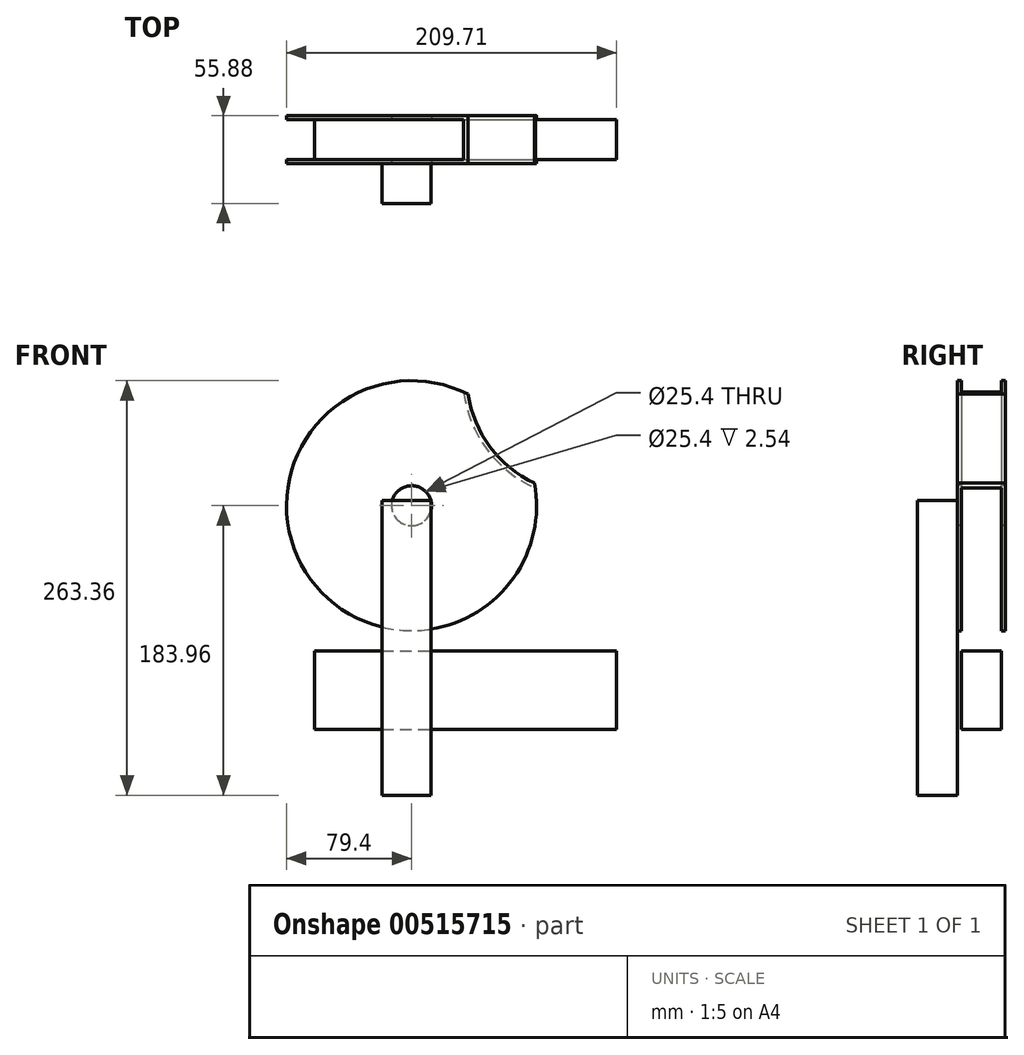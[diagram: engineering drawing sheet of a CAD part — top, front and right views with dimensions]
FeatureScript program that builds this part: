
annotation { "Feature Type Name" : "Feature", "Feature Type Description" : "" }
export const myFeature = defineFeature(function(context is Context, id is Id, definition is map)
    precondition{}
    {
        {
            var Q0;
            Q0=qCreatedBy(makeId("Front.planeOp"),FACE);
            var sketch = newSketch(context, id + "F0", { "sketchPlane" : qUnion([Q0])});
            skCircle(sketch, "E0", {"center": v(0, 0) * mm, "radius": 76.98 * mm});
            skSolve(sketch);
        }
        {
            var Q0;
            Q0 = qSketchRegion(id + "F0", true);
            var sketch = newSketch(context, id + "F1", { "sketchPlane" : qUnion([Q0])});
            skCircle(sketch, "E1", {"center": v(-109.51, -81.83) * mm, "radius": 79.4 * mm});
            skSolve(sketch);
        }
        {
            var Q0;
            {var subQ0=sQuery(id+"F1.wireOp",EDGE,"E1");var subQ1=makeQuery(id+"F0.imprint","IMPRINT",EDGE,{"derivedFrom":sQuery(id+"F0.wireOp",EDGE,"E0")});var subQ2=makeQuery(id+"F1.imprint","INTERSECT",VERTEX,{"disambiguationData":[OD(0.0)],"derivedFrom":[subQ1,subQ0]});Q0=makeQuery(id+"F1.imprint","IMPRINT",FACE,{"disambiguationData":[TD([[makeQuery(id+"F1.imprint","IMPRINT",EDGE,{"disambiguationData":[TD([[subQ2,-1.0]])],"derivedFrom":subQ0}),1.0]])]});}
            var sketch = newSketch(context, id + "F2", { "sketchPlane" : qUnion([Q0])});
            skPoint(sketch, "E2", {"position": v(-107.6, -82.06) * mm});
            skPoint(sketch, "E3", {"position": v(-2.08, -7.32) * mm});
            skPoint(sketch, "E4", {"position": v(-0.4, -0.73) * mm});
            skPoint(sketch, "E5", {"position": v(-1.37, 2.2) * mm});
            skPoint(sketch, "E6", {"position": v(-3.44, 2.31) * mm});
            skPoint(sketch, "E7", {"position": v(38.83, 49.92) * mm});
            skPoint(sketch, "E8", {"position": v(-53.49, -51.53) * mm});
            skPoint(sketch, "E9", {"position": v(5.53, -11.82) * mm});
            skPoint(sketch, "E10", {"position": v(-116.54, -130.64) * mm});
            skSolve(sketch);
        }
        {
            var Q0;
            Q0 = qSketchRegion(id + "F2", true);
            var Q1;
            {var subQ0=sQuery(id+"F1.wireOp",EDGE,"E1");var subQ1=makeQuery(id+"F0.imprint","IMPRINT",EDGE,{"derivedFrom":sQuery(id+"F0.wireOp",EDGE,"E0")});var subQ2=makeQuery(id+"F1.imprint","INTERSECT",VERTEX,{"disambiguationData":[OD(0.0)],"derivedFrom":[subQ1,subQ0]});Q1=makeQuery(id+"F1.imprint","IMPRINT",FACE,{"disambiguationData":[TD([[makeQuery(id+"F1.imprint","IMPRINT",EDGE,{"disambiguationData":[TD([[subQ2,-1.0]])],"derivedFrom":subQ0}),1.0]])]});}
            extrude(context, id + "F3", {"entities" : qUnion([Q0, Q1]), "depth" : 25.4 * mm, "offsetDistance" : 25.4 * mm});
        }
        {
            var Q0;
            Q0=makeQuery(id+"F3.opExtrude","CAP_FACE",FACE,{"disambiguationData":[OSD([sQuery(id+"F0.wireOp",EDGE,"E0"),sQuery(id+"F1.wireOp",EDGE,"E1")])],"isStart":true});
            chamfer(context, id + "F4", {"entities" : qUnion([Q0]), "width" : 5.08 * mm, "tangentPropagation" : true});
        }
        {
            var Q0;
            Q0=sQuery(id+"F0.wireOp",EDGE,"E0");
            extrude(context, id + "F5", {"bodyType" : ToolBodyType.SURFACE, "surfaceEntities" : qUnion([Q0]), "depth" : 25.4 * mm, "offsetDistance" : 25.4 * mm});
        }
        {
            var Q1;
            Q1=makeQuery(id+"F3.opExtrude","CAP_FACE",FACE,{"disambiguationData":[OSD([sQuery(id+"F0.wireOp",EDGE,"E0"),sQuery(id+"F1.wireOp",EDGE,"E1")])],"isStart":false});
            var Q2;
            {var subQ0=sQuery(id+"F1.wireOp",EDGE,"E1");var subQ1=makeQuery(id+"F0.imprint","IMPRINT",EDGE,{"derivedFrom":sQuery(id+"F0.wireOp",EDGE,"E0")});var subQ2=makeQuery(id+"F1.imprint","INTERSECT",VERTEX,{"disambiguationData":[OD(0.0)],"derivedFrom":[subQ1,subQ0]});Q2=makeQuery(id+"F2.imprint","IMPRINT",FACE,{"disambiguationData":[TD([[makeQuery(id+"F2.imprint","IMPRINT",EDGE,{"derivedFrom":makeQuery(id+"F1.imprint","IMPRINT",EDGE,{"disambiguationData":[TD([[subQ2,-1.0]])],"derivedFrom":subQ0})}),1.0]])]});}
            loft(context, id + "F6", {"operationType" : NewBodyOperationType.ADD, "sheetProfilesArray" : [{ "sheetProfileEntities" : qUnion([Q1]) }, { "sheetProfileEntities" : qUnion([Q2]) }]});
        }
        {
            var Q0;
            {var subQ0=sQuery(id+"F1.wireOp",EDGE,"E1");var subQ1=sQuery(id+"F0.wireOp",EDGE,"E0");var subQ2=makeQuery(id+"F0.imprint","IMPRINT",EDGE,{"derivedFrom":subQ1});var subQ3=makeQuery(id+"F1.imprint","INTERSECT",VERTEX,{"disambiguationData":[OD(1.0)],"derivedFrom":[subQ2,subQ0]});var subQ4=makeQuery(id+"F1.imprint","INTERSECT",VERTEX,{"disambiguationData":[OD(0.0)],"derivedFrom":[subQ2,subQ0]});var subQ5=makeQuery(id+"F1.imprint","IMPRINT",EDGE,{"disambiguationData":[TD([[subQ4,-1.0]])],"derivedFrom":subQ0});var subQ6=makeQuery(id+"F1.imprint","IMPRINT",EDGE,{"disambiguationData":[TD([[subQ4,-1.0]])],"derivedFrom":subQ2});Q0=makeQuery(id+"F6.boolean.opBoolean","MERGE",FACE,{"derivedFrom":[makeQuery(id+"F3.opExtrude","SWEPT_FACE",FACE,{"disambiguationData":[OSD([subQ0])]}),makeQuery(id+"F6.opLoft","SWEPT_FACE",FACE,{"disambiguationData":[OSD([subQ1,subQ0]),TDD([makeQuery(id+"F2.imprint","INTERSECT",VERTEX,{"disambiguationData":[OD(0.0)],"derivedFrom":[subQ5,subQ6]}),makeQuery(id+"F2.imprint","INTERSECT",VERTEX,{"disambiguationData":[OD(1.0)],"derivedFrom":[subQ5,subQ6]}),makeQuery(id+"F2.imprint","IMPRINT",EDGE,{"derivedFrom":subQ5}),makeQuery(id+"F3.opExtrude","CAP_VERTEX",VERTEX,{"disambiguationData":[OSD([subQ1,subQ0]),TDD([subQ4])],"isStart":false}),makeQuery(id+"F3.opExtrude","CAP_VERTEX",VERTEX,{"disambiguationData":[OSD([subQ1,subQ0]),TDD([subQ3])],"isStart":false}),makeQuery(id+"F3.opExtrude","CAP_EDGE",EDGE,{"disambiguationData":[OSD([subQ0])],"isStart":false})])]})]});}
            shell(context, id + "F7", {"entities" : qUnion([Q0]), "thickness" : 2.54 * mm, "oppositeDirection" : true});
        }
        {
            var Q0;
            Q0=makeQuery(id+"F3.opExtrude","CAP_FACE",FACE,{"disambiguationData":[OSD([sQuery(id+"F0.wireOp",EDGE,"E0"),sQuery(id+"F1.wireOp",EDGE,"E1")])],"isStart":false});
            var sketch = newSketch(context, id + "F8", { "sketchPlane" : qUnion([Q0])});
            skPoint(sketch, "E11", {"position": v(-109.51, -81.83) * mm});
            skSolve(sketch);
        }
        {
            var Q0;
            Q0=sQuery(id+"F8.wireOp",VERTEX,"E11");
            var Q1;
            Q1=makeQuery(id+"F3.opExtrude","SWEPT_BODY",BODY,{"disambiguationData":[OSD([sQuery(id+"F0.wireOp",EDGE,"E0"),sQuery(id+"F1.wireOp",EDGE,"E1")])]});
            hole(context, id + "F9", {"style" : HoleStyle.C_SINK, "endStyle" : HoleEndStyle.THROUGH, "standardTappedOrClearance" : lookupTablePath({ "fit" : "Normal (ASME)", "standard" : "ANSI", "engagement" : "75%", "pitch" : "20 tpi", "size" : "1 (1)", "type" : "Drilled" }), "standardBlindInLast" : lookupTablePath({ "fit" : "Free", "standard" : "ANSI", "engagement" : "75%", "pitch" : "20 tpi", "size" : "1", "type" : "Drilled" }), "holeDiameter" : 25.4 * mm, "cSinkDiameter" : 25.4 * mm, "cSinkAngle" : 82 * degree, "showTappedDepth" : true, "isTappedThrough" : true, "tappedDepth" : 12.7 * mm, "tapClearance" : 3, "locations" : qUnion([Q0]), "scope" : qUnion([Q1])});
        }
        {
            var Q0;
            Q0=makeQuery(id+"F3.opExtrude","CAP_FACE",FACE,{"disambiguationData":[OSD([sQuery(id+"F0.wireOp",EDGE,"E0"),sQuery(id+"F1.wireOp",EDGE,"E1")])],"isStart":false});
            var sketch = newSketch(context, id + "F10", { "sketchPlane" : qUnion([Q0])});
            skLineSegment(sketch, "E12.bottom", {"start": v(-97.23, -78.6) * mm, "end": v(-128.39, -78.6) * mm});
            skLineSegment(sketch, "E12.top", {"start": v(-97.23, -265.79) * mm, "end": v(-128.39, -265.79) * mm});
            skLineSegment(sketch, "E12.left", {"start": v(-97.23, -78.6) * mm, "end": v(-97.23, -265.79) * mm});
            skLineSegment(sketch, "E12.right", {"start": v(-128.39, -78.6) * mm, "end": v(-128.39, -265.79) * mm});
            skSolve(sketch);
        }
        {
            var Q0;
            Q0 = qSketchRegion(id + "F10", true);
            extrude(context, id + "F11", {"entities" : qUnion([Q0]), "operationType" : NewBodyOperationType.ADD, "depth" : 25.4 * mm, "offsetDistance" : 25.4 * mm});
        }
        {
            var Q0;
            Q0=qCreatedBy(makeId("Front.planeOp"),FACE);
            var sketch = newSketch(context, id + "F12", { "sketchPlane" : qUnion([Q0])});
            skLineSegment(sketch, "E13.bottom", {"start": v(-171.06, -174.16) * mm, "end": v(20.8, -174.16) * mm});
            skLineSegment(sketch, "E13.top", {"start": v(-171.06, -223.87) * mm, "end": v(20.8, -223.87) * mm});
            skLineSegment(sketch, "E13.left", {"start": v(-171.06, -174.16) * mm, "end": v(-171.06, -223.87) * mm});
            skLineSegment(sketch, "E13.right", {"start": v(20.8, -174.16) * mm, "end": v(20.8, -223.87) * mm});
            skSolve(sketch);
        }
        {
            var Q0;
            Q0=makeQuery(id+"F12.imprint","IMPRINT",FACE,{"disambiguationData":[TD([[makeQuery(id+"F12.imprint","IMPRINT",EDGE,{"derivedFrom":sQuery(id+"F12.wireOp",EDGE,"E13.bottom")}),-1.0]])]});
            var sketch = newSketch(context, id + "F13", { "sketchPlane" : qUnion([Q0])});
            skSolve(sketch);
        }
        {
            var Q0;
            Q0=makeQuery(id+"F13.imprint","IMPRINT",FACE,{"disambiguationData":[TD([[makeQuery(id+"F13.imprint","IMPRINT",EDGE,{"derivedFrom":makeQuery(id+"F12.imprint","IMPRINT",EDGE,{"derivedFrom":sQuery(id+"F12.wireOp",EDGE,"E13.bottom")})}),-1.0]])]});
            extrude(context, id + "F14", {"entities" : qUnion([Q0]), "depth" : 25.4 * mm, "offsetDistance" : 25.4 * mm});
        }
    });
